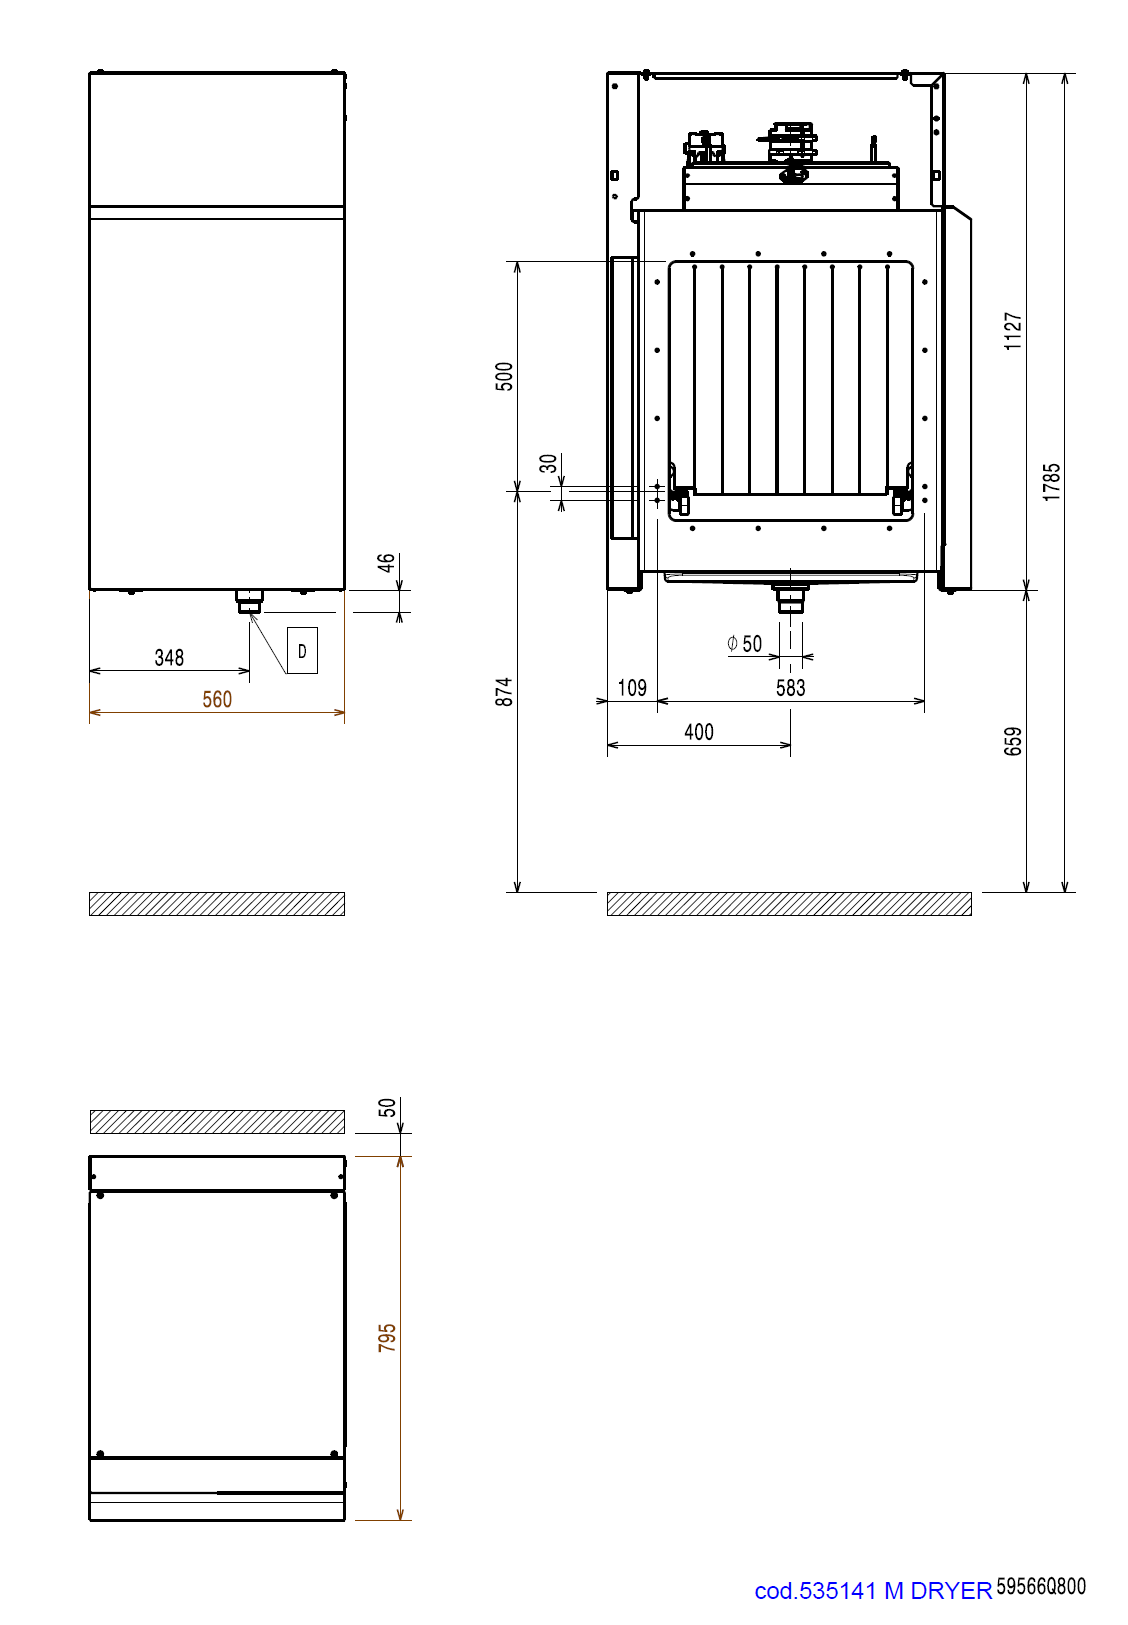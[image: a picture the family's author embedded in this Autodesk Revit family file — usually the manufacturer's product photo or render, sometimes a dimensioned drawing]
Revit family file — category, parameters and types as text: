
# Revit family: QF_ELECTROLUXPROFESSIONAL_535135_NMHABDR5M
name_source: partatom
category: Specialty Equipment
revit_build: Autodesk Revit 2018 (Build: 20190510_1515(x64)
units: mm (PartAtom-declared; Revit-internal decimal feet)

## family parameters
Always vertical = Yes
Cut with Voids When Loaded = No
Part Type = Normal
Room Calculation Point = No
Round Connector Dimension = Use Diameter
Shared = No
Work Plane-Based = No

## types (2) — shared parameters
Accessory = Yes
Cold Water Size = 0 mm
Compressed Air Pressure = 0.0 Pa
Compressed Air Size = 0 mm
Compressed Air Volume = 0.0 L/s
Condensate Return Size = 0 mm
Depth Actual = 795 mm  [stored 2.60827 ft]
Direct Waste Size = 50 mm
Gas Input Pressure = 0
Gas Size = 0 mm
HP = 5.9 HP
Height Actual = 1130 mm  [stored 3.70735 ft]
Hot Water Size = 0 mm
Length Actual = 560 mm  [stored 1.83727 ft]
Refrigerant Compressor Remote = Yes
Refrigeration Liquid Line Size = 0 mm
Refrigeration Suction Line Size = 0 mm
Steam Supply Maximum Pressure = 0.0 Pa
Steam Supply Minimum Pressure = 0.0 Pa
Steam Supply Size = 0 mm
URL = http://professional.electrolux.com
Watts = 0 W
Weight = 0.00 kg
zero-valued in all types: Gas KW, Steam Pounds per Hour

## per-type parameters (varying)
| type | Cycle | Description | Item Number | Manufacturer | Model | Phase | URL Manufacturer | Volts |
| NMHDRE56 | 0 Hz | SINGLE RINSE RT, 100R/H, ELECTRIC 50HZ |  | Electrolux | ESR10E5 | 0 |  | 0 V |
| Standard | 50 Hz | MEDIUM DRYER WITHOUT DOOR (HAB), DUAL RINSE RT, ELECTRIC, 400V/ 3/ 50Hz-MARINE | 535135 | Electrolux Professional | NMHABDR5M | 3 | http://professional.electrolux.com | 400 V |

note: source unit labels omitted for Gas Input Pressure — the stored unit's dimension contradicts the parameter name (converter mislabeling)

note: [stored X ft] marks values corroborated as IEEE doubles in the binary element streams (Revit-internal decimal feet)
